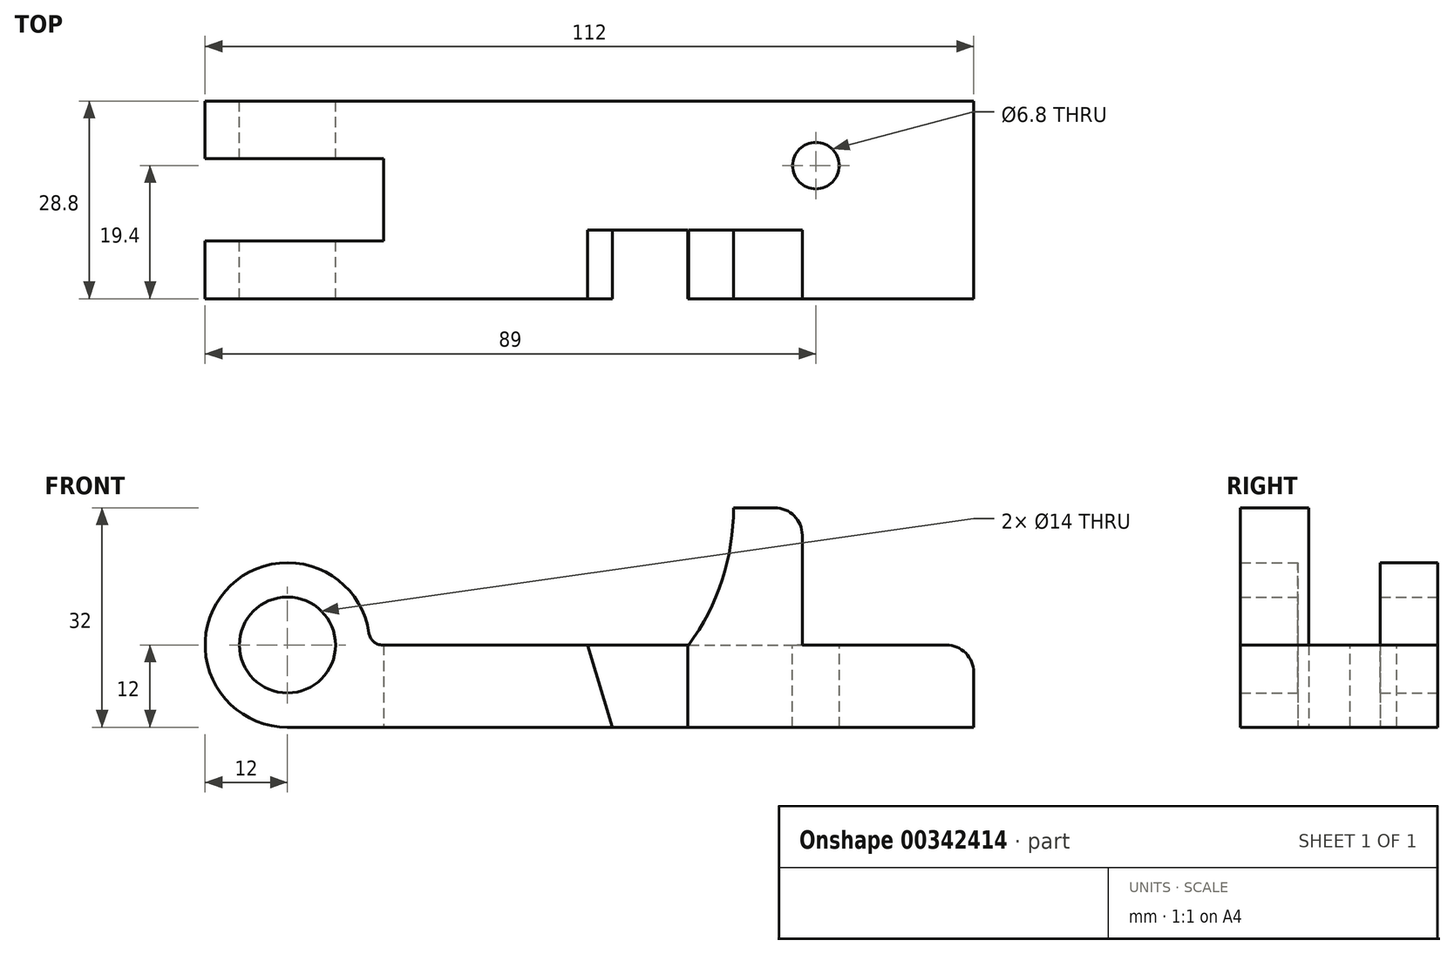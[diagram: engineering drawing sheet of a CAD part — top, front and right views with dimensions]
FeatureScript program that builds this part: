
annotation { "Feature Type Name" : "Feature", "Feature Type Description" : "" }
export const myFeature = defineFeature(function(context is Context, id is Id, definition is map)
    precondition{}
    {
        {
            var Q0;
            Q0=qCreatedBy(makeId("Front.planeOp"),FACE);
            var sketch = newSketch(context, id + "F0", { "sketchPlane" : qUnion([Q0])});
            skArc(sketch, "E0", {"start": v(12, 0) * mm, "mid": v(-8.49, 8.49) * mm, "end": v(0, -12) * mm});
            skCircle(sketch, "E1", {"center": v(0, 0) * mm, "radius": 7 * mm});
            skLineSegment(sketch, "E2.top", {"start": v(0, -12) * mm, "end": v(100, -12) * mm});
            skLineSegment(sketch, "E2.right", {"start": v(100, 0) * mm, "end": v(100, -12) * mm});
            skLineSegment(sketch, "E3.trimOffspring", {"start": v(12, 0) * mm, "end": v(100, 0) * mm});
            skSolve(sketch);
        }
        {
            var Q0;
            Q0=makeQuery(id+"F0.imprint","IMPRINT",FACE,{"disambiguationData":[TD([[makeQuery(id+"F0.imprint","IMPRINT",EDGE,{"derivedFrom":sQuery(id+"F0.wireOp",EDGE,"E0")}),1.0]])]});
            extrude(context, id + "F1", {"entities" : qUnion([Q0]), "endBound" : BoundingType.SYMMETRIC, "depth" : 28.8 * mm});
        }
        {
            var Q0;
            Q0=qCreatedBy(makeId("Front.planeOp"),FACE);
            var sketch = newSketch(context, id + "F2", { "sketchPlane" : qUnion([Q0])});
            skLineSegment(sketch, "E4", {"start": v(14, 0) * mm, "end": v(14, -12) * mm});
            skArc(sketch, "E5.0", {"start": v(12, 0) * mm, "mid": v(-8.49, 8.49) * mm, "end": v(0, -12) * mm});
            skLineSegment(sketch, "E6", {"start": v(12, 0) * mm, "end": v(14, 0) * mm});
            skLineSegment(sketch, "E7", {"start": v(0, -12) * mm, "end": v(14, -12) * mm});
            skSolve(sketch);
        }
        {
            var Q0;
            Q0=makeQuery(id+"F1.opExtrude","CAP_FACE",FACE,{"disambiguationData":[OSD([sQuery(id+"F0.wireOp",EDGE,"E0"),sQuery(id+"F0.wireOp",EDGE,"E1"),sQuery(id+"F0.wireOp",EDGE,"E2.top"),sQuery(id+"F0.wireOp",EDGE,"E2.right"),sQuery(id+"F0.wireOp",EDGE,"E3.trimOffspring")])],"isStart":false});
            var sketch = newSketch(context, id + "F3", { "sketchPlane" : qUnion([Q0])});
            skLineSegment(sketch, "E8.bottom", {"start": v(75, 0) * mm, "end": v(65, 0) * mm});
            skLineSegment(sketch, "E8.top", {"start": v(75, 20) * mm, "end": v(65, 20) * mm});
            skLineSegment(sketch, "E8.left", {"start": v(75, 0) * mm, "end": v(75, 20) * mm});
            skArc(sketch, "E9", {"start": v(58.48, 0) * mm, "mid": v(63.33, 9.48) * mm, "end": v(65, 20) * mm});
            skLineSegment(sketch, "E10", {"start": v(58.48, 0) * mm, "end": v(65, 0) * mm});
            skSolve(sketch);
        }
        {
            var Q0;
            Q0=makeQuery(id+"F3.imprint","IMPRINT",FACE,{"disambiguationData":[TD([[makeQuery(id+"F3.imprint","IMPRINT",EDGE,{"derivedFrom":sQuery(id+"F3.wireOp",EDGE,"E8.bottom")}),1.0]])]});
            extrude(context, id + "F4", {"entities" : qUnion([Q0]), "operationType" : NewBodyOperationType.ADD, "oppositeDirection" : true, "depth" : 10 * mm});
        }
        {
            var Q0;
            Q0=makeQuery(id+"F4.boolean.opBoolean","MERGE",FACE,{"derivedFrom":[makeQuery(id+"F1.opExtrude","CAP_FACE",FACE,{"disambiguationData":[OSD([sQuery(id+"F0.wireOp",EDGE,"E0"),sQuery(id+"F0.wireOp",EDGE,"E1"),sQuery(id+"F0.wireOp",EDGE,"E2.top"),sQuery(id+"F0.wireOp",EDGE,"E2.right"),sQuery(id+"F0.wireOp",EDGE,"E3.trimOffspring")])],"isStart":false}),makeQuery(id+"F4.opExtrude","CAP_FACE",FACE,{"disambiguationData":[OSD([sQuery(id+"F3.wireOp",EDGE,"E8.bottom"),sQuery(id+"F3.wireOp",EDGE,"E8.top"),sQuery(id+"F3.wireOp",EDGE,"E8.left"),sQuery(id+"F3.wireOp",EDGE,"E9"),sQuery(id+"F3.wireOp",EDGE,"E10")])],"isStart":true})]});
            var sketch = newSketch(context, id + "F5", { "sketchPlane" : qUnion([Q0])});
            skSolve(sketch);
        }
        {
            var Q0;
            {var subQ3=sQuery(id+"F0.wireOp",EDGE,"E0");Q0=makeQuery(id+"F5.imprint","IMPRINT",FACE,{"disambiguationData":[TD([[makeQuery(id+"F5.imprint","IMPRINT",EDGE,{"derivedFrom":makeQuery(id+"F1.opExtrude","CAP_EDGE",EDGE,{"disambiguationData":[OSD([subQ3])],"isStart":false})}),1.0]])]});}
            var sketch = newSketch(context, id + "F6", { "sketchPlane" : qUnion([Q0])});
            skLineSegment(sketch, "E11", {"start": v(58.35, 0) * mm, "end": v(58.35, -12.36) * mm});
            skLineSegment(sketch, "E12", {"start": v(58.35, -12.36) * mm, "end": v(47.46, -12.36) * mm});
            skLineSegment(sketch, "E13", {"start": v(47.46, -12.36) * mm, "end": v(43.7, 0) * mm});
            skSolve(sketch);
        }
        {
            var Q0;
            {var subQ0=sQuery(id+"F6.wireOp",EDGE,"E11");var subQ2=sQuery(id+"F0.wireOp",EDGE,"E2.top");var subQ7=makeQuery(id+"F5.imprint","IMPRINT",EDGE,{"derivedFrom":makeQuery(id+"F1.opExtrude","CAP_EDGE",EDGE,{"disambiguationData":[OSD([subQ2])],"isStart":false})});var subQ8=makeQuery(id+"F6.imprint","INTERSECT",VERTEX,{"derivedFrom":[subQ7,subQ0]});Q0=makeQuery(id+"F6.imprint","IMPRINT",FACE,{"disambiguationData":[TD([[makeQuery(id+"F6.imprint","IMPRINT",EDGE,{"disambiguationData":[TD([[subQ8,1.0]])],"derivedFrom":subQ7}),1.0]])]});}
            extrude(context, id + "F7", {"entities" : qUnion([Q0]), "operationType" : NewBodyOperationType.REMOVE, "oppositeDirection" : true, "depth" : 10 * mm});
        }
        {
            var Q0;
            Q0 = qSketchRegion(id + "F2", true);
            extrude(context, id + "F8", {"entities" : qUnion([Q0]), "operationType" : NewBodyOperationType.REMOVE, "endBound" : BoundingType.SYMMETRIC, "oppositeDirection" : true, "depth" : 12 * mm});
        }
        {
            var Q0;
            Q0=makeQuery(id+"F1.opExtrude","SWEPT_FACE",FACE,{"disambiguationData":[OSD([sQuery(id+"F0.wireOp",EDGE,"E3.trimOffspring")])]});
            var sketch = newSketch(context, id + "F9", { "sketchPlane" : qUnion([Q0])});
            skCircle(sketch, "E14", {"center": v(77, 5) * mm, "radius": 3.4 * mm});
            skSolve(sketch);
        }
        {
            var Q0;
            Q0 = qSketchRegion(id + "F9", true);
            extrude(context, id + "F10", {"entities" : qUnion([Q0]), "operationType" : NewBodyOperationType.REMOVE, "oppositeDirection" : true, "depth" : 25 * mm});
        }
        {
            var Q0;
            Q0=makeQuery(id+"F1.opExtrude","SWEPT_EDGE",EDGE,{"disambiguationData":[OSD([sQuery(id+"F0.wireOp",EDGE,"E2.right"),sQuery(id+"F0.wireOp",EDGE,"E3.trimOffspring")])]});
            var Q1;
            Q1=makeQuery(id+"F4.opExtrude","SWEPT_EDGE",EDGE,{"disambiguationData":[OSD([sQuery(id+"F3.wireOp",EDGE,"E8.top"),sQuery(id+"F3.wireOp",EDGE,"E8.left")])]});
            fillet(context, id + "F11", {"entities" : qUnion([Q0, Q1]), "radius" : 4 * mm, "tangentPropagation" : true, "allowEdgeOverflow" : false});
        }
        {
            var Q0;
            Q0=makeQuery(id+"F4.opExtrude","SWEPT_EDGE",EDGE,{"disambiguationData":[OSD([sQuery(id+"F0.wireOp",EDGE,"E3.trimOffspring"),sQuery(id+"F3.wireOp",EDGE,"E8.bottom"),sQuery(id+"F3.wireOp",EDGE,"E8.left")])]});
            var Q1;
            {var subQ0=sQuery(id+"F0.wireOp",EDGE,"E0");var subQ1=sQuery(id+"F0.wireOp",EDGE,"E3.trimOffspring");Q1=makeQuery(id+"F8.boolean.opBoolean","SPLIT",EDGE,{"disambiguationData":[TD([makeQuery(id+"F8.opExtrude","CAP_FACE",FACE,{"disambiguationData":[OSD([sQuery(id+"F2.wireOp",EDGE,"E4"),sQuery(id+"F2.wireOp",EDGE,"E5.0"),sQuery(id+"F2.wireOp",EDGE,"E6"),sQuery(id+"F2.wireOp",EDGE,"E7")])],"isStart":false})])],"derivedFrom":makeQuery(id+"F1.opExtrude","SWEPT_EDGE",EDGE,{"disambiguationData":[OSD([subQ0,subQ1])]})});}
            var Q2;
            {var subQ0=sQuery(id+"F0.wireOp",EDGE,"E3.trimOffspring");var subQ1=sQuery(id+"F0.wireOp",EDGE,"E0");Q2=makeQuery(id+"F8.boolean.opBoolean","SPLIT",EDGE,{"disambiguationData":[TD([makeQuery(id+"F8.opExtrude","CAP_FACE",FACE,{"disambiguationData":[OSD([sQuery(id+"F2.wireOp",EDGE,"E4"),sQuery(id+"F2.wireOp",EDGE,"E5.0"),sQuery(id+"F2.wireOp",EDGE,"E6"),sQuery(id+"F2.wireOp",EDGE,"E7")])],"isStart":true})])],"derivedFrom":makeQuery(id+"F1.opExtrude","SWEPT_EDGE",EDGE,{"disambiguationData":[OSD([subQ1,subQ0])]})});}
            fillet(context, id + "F12", {"entities" : qUnion([Q0, Q1, Q2]), "radius" : 2 * mm, "tangentPropagation" : true, "allowEdgeOverflow" : false});
        }
    });
